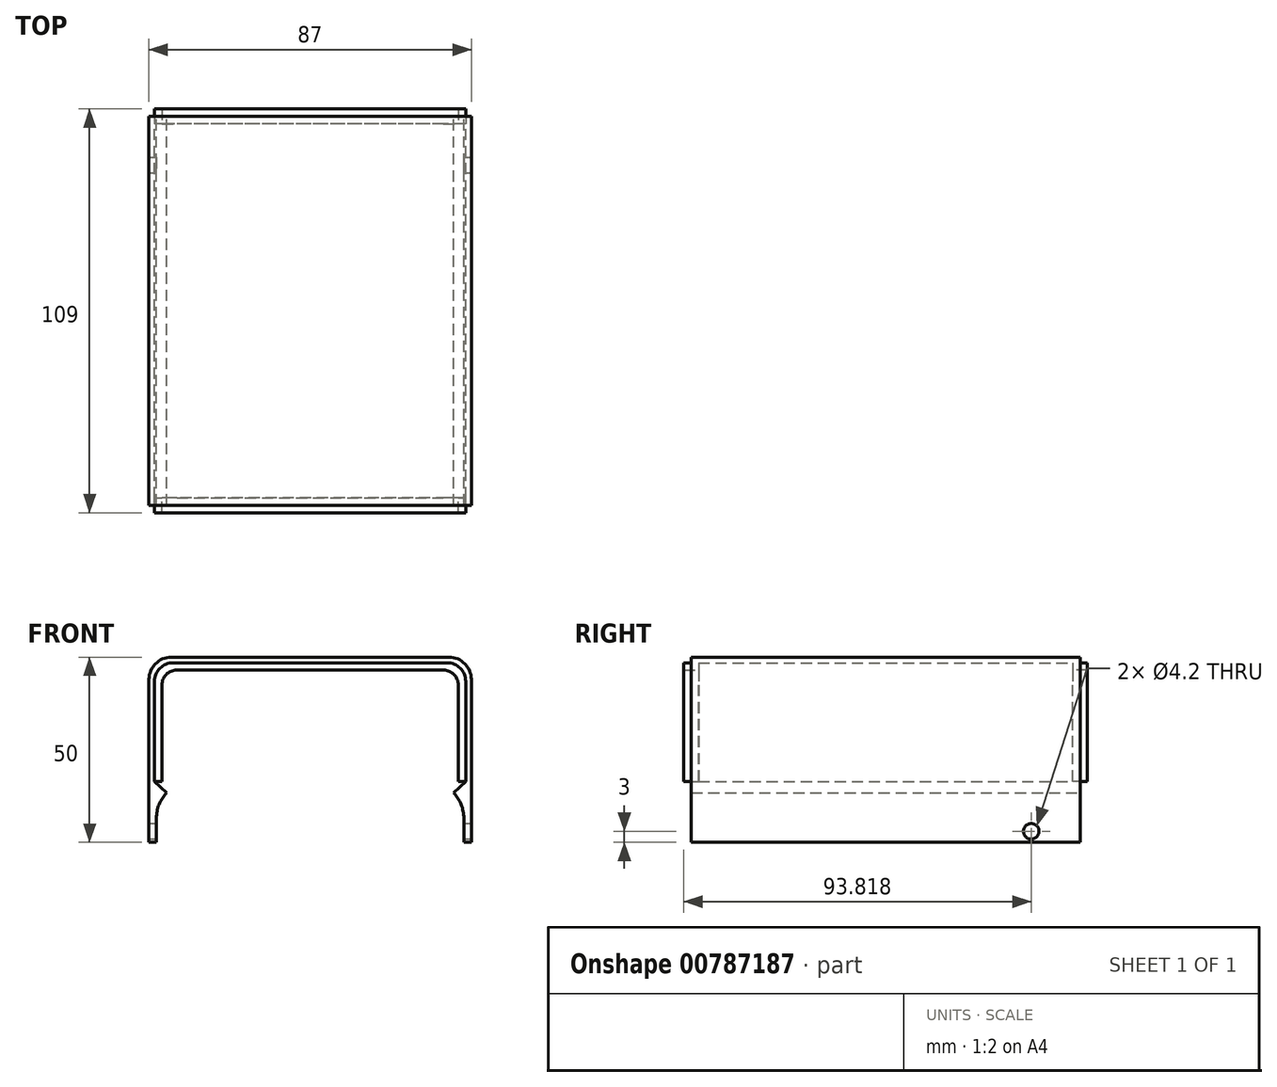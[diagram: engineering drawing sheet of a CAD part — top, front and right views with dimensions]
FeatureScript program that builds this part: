
annotation { "Feature Type Name" : "Feature", "Feature Type Description" : "" }
export const myFeature = defineFeature(function(context is Context, id is Id, definition is map)
    precondition{}
    {
        {
            var Q0;
            Q0=qCreatedBy(makeId("Front.planeOp"),FACE);
            var sketch = newSketch(context, id + "F0", { "sketchPlane" : qUnion([Q0])});
            skLineSegment(sketch, "E0.bottom", {"start": v(-31.5, 21.5) * mm, "end": v(31.5, 21.5) * mm});
            skLineSegment(sketch, "E0.top", {"start": v(-41.5, -21.5) * mm, "end": v(41.5, -21.5) * mm});
            skLineSegment(sketch, "E0.left", {"start": v(-41.5, 11.5) * mm, "end": v(-41.5, -21.5) * mm});
            skLineSegment(sketch, "E0.right", {"start": v(41.5, 11.5) * mm, "end": v(41.5, -21.5) * mm});
            skPoint(sketch, "E0.middle", {"position": v(0, 0) * mm});
            skPoint(sketch, "E1.visualSharp", {"position": v(-41.5, 21.5) * mm});
            skArc(sketch, "E1.filletArc", {"start": v(-31.5, 21.5) * mm, "mid": v(-38.57, 18.57) * mm, "end": v(-41.5, 11.5) * mm});
            skPoint(sketch, "E2.visualSharp", {"position": v(41.5, 21.5) * mm});
            skArc(sketch, "E2.filletArc", {"start": v(41.5, 11.5) * mm, "mid": v(38.57, 18.57) * mm, "end": v(31.5, 21.5) * mm});
            skLineSegment(sketch, "E3", {"start": v(-41.5, 5) * mm, "end": v(-43.5, 5) * mm});
            skLineSegment(sketch, "E4", {"start": v(-43.5, 49) * mm, "end": v(-43.5, 5) * mm});
            skLineSegment(sketch, "E5", {"start": v(41.5, 5) * mm, "end": v(43.5, 5) * mm});
            skLineSegment(sketch, "E6", {"start": v(43.5, 49) * mm, "end": v(43.5, 5) * mm});
            skLineSegment(sketch, "E7", {"start": v(37.5, 55) * mm, "end": v(-37.5, 55) * mm});
            skLineSegment(sketch, "E8", {"start": v(-31.5, 21.5) * mm, "end": v(-42, 21.5) * mm});
            skLineSegment(sketch, "E9", {"start": v(-42, 21.5) * mm, "end": v(-42, 48.5) * mm});
            skLineSegment(sketch, "E10", {"start": v(31.5, 21.5) * mm, "end": v(42, 21.5) * mm});
            skLineSegment(sketch, "E11", {"start": v(42, 21.5) * mm, "end": v(42, 48.5) * mm});
            skLineSegment(sketch, "E12", {"start": v(37, 53.5) * mm, "end": v(-37, 53.5) * mm});
            skPoint(sketch, "E13.visualSharp", {"position": v(-42, 53.5) * mm});
            skArc(sketch, "E13.filletArc", {"start": v(-37, 53.5) * mm, "mid": v(-40.54, 52.04) * mm, "end": v(-42, 48.5) * mm});
            skPoint(sketch, "E14.visualSharp", {"position": v(42, 53.5) * mm});
            skArc(sketch, "E14.filletArc", {"start": v(42, 48.5) * mm, "mid": v(40.54, 52.04) * mm, "end": v(37, 53.5) * mm});
            skPoint(sketch, "E15.visualSharp", {"position": v(-43.5, 55) * mm});
            skArc(sketch, "E15.filletArc", {"start": v(-37.5, 55) * mm, "mid": v(-41.74, 53.24) * mm, "end": v(-43.5, 49) * mm});
            skPoint(sketch, "E16.visualSharp", {"position": v(43.5, 55) * mm});
            skArc(sketch, "E16.filletArc", {"start": v(43.5, 49) * mm, "mid": v(41.74, 53.24) * mm, "end": v(37.5, 55) * mm});
            skLineSegment(sketch, "E17", {"start": v(-42, 21.5) * mm, "end": v(-31.5, 11.5) * mm});
            skLineSegment(sketch, "E18", {"start": v(42, 21.5) * mm, "end": v(31.5, 11.5) * mm});
            skSolve(sketch);
        }
        {
            var Q0;
            {var subQ2=sQuery(id+"F0.wireOp",EDGE,"E3");Q0=makeQuery(id+"F0.imprint","IMPRINT",FACE,{"disambiguationData":[TD([[makeQuery(id+"F0.imprint","IMPRINT",EDGE,{"derivedFrom":subQ2}),-1.0]])]});}
            extrude(context, id + "F1", {"entities" : qUnion([Q0]), "depth" : 105 * mm, "offsetDistance" : 25 * mm});
        }
        {
            var Q0;
            Q0=makeQuery(id+"F1.opExtrude","SWEPT_FACE",FACE,{"disambiguationData":[OSD([sQuery(id+"F0.wireOp",EDGE,"E6")])]});
            var sketch = newSketch(context, id + "F2", { "sketchPlane" : qUnion([Q0])});
            skCircle(sketch, "E19", {"center": v(-13.18, 8) * mm, "radius": 2.1 * mm});
            skSolve(sketch);
        }
        {
            var Q0;
            Q0=makeQuery(id+"F2.imprint","IMPRINT",FACE,{"disambiguationData":[TD([[makeQuery(id+"F2.imprint","IMPRINT",EDGE,{"derivedFrom":sQuery(id+"F2.wireOp",EDGE,"E19")}),1.0]])]});
            extrude(context, id + "F3", {"entities" : qUnion([Q0]), "operationType" : NewBodyOperationType.REMOVE, "endBound" : BoundingType.THROUGH_ALL, "oppositeDirection" : true, "depth" : 25 * mm, "offsetDistance" : 25 * mm});
        }
        {
            var Q0;
            Q0=makeQuery(id+"F1.opExtrude","CAP_FACE",FACE,{"disambiguationData":[OSD([sQuery(id+"F0.wireOp",EDGE,"E0.left"),sQuery(id+"F0.wireOp",EDGE,"E0.right"),sQuery(id+"F0.wireOp",EDGE,"E1.filletArc"),sQuery(id+"F0.wireOp",EDGE,"E2.filletArc"),sQuery(id+"F0.wireOp",EDGE,"E3"),sQuery(id+"F0.wireOp",EDGE,"E4"),sQuery(id+"F0.wireOp",EDGE,"E5"),sQuery(id+"F0.wireOp",EDGE,"E6"),sQuery(id+"F0.wireOp",EDGE,"E7"),sQuery(id+"F0.wireOp",EDGE,"E9"),sQuery(id+"F0.wireOp",EDGE,"E11"),sQuery(id+"F0.wireOp",EDGE,"E12"),sQuery(id+"F0.wireOp",EDGE,"E13.filletArc"),sQuery(id+"F0.wireOp",EDGE,"E14.filletArc"),sQuery(id+"F0.wireOp",EDGE,"E15.filletArc"),sQuery(id+"F0.wireOp",EDGE,"E16.filletArc"),sQuery(id+"F0.wireOp",EDGE,"E17"),sQuery(id+"F0.wireOp",EDGE,"E18")])],"isStart":true});
            var sketch = newSketch(context, id + "F4", { "sketchPlane" : qUnion([Q0])});
            skLineSegment(sketch, "E20.0", {"start": v(-37.5, 55) * mm, "end": v(37.5, 55) * mm});
            skArc(sketch, "E21.0", {"start": v(-43.5, 49) * mm, "mid": v(-41.74, 53.24) * mm, "end": v(-37.5, 55) * mm});
            skArc(sketch, "E22.0", {"start": v(37.5, 55) * mm, "mid": v(41.74, 53.24) * mm, "end": v(43.5, 49) * mm});
            skLineSegment(sketch, "E23.0", {"start": v(-43.5, 49) * mm, "end": v(-43.5, 5) * mm});
            skLineSegment(sketch, "E24.0", {"start": v(43.5, 49) * mm, "end": v(43.5, 5) * mm});
            skLineSegment(sketch, "E25", {"start": v(-43.5, 5) * mm, "end": v(43.5, 5) * mm});
            skSolve(sketch);
        }
        {
            var Q0;
            Q0=makeQuery(id+"F1.opExtrude","CAP_FACE",FACE,{"disambiguationData":[OSD([sQuery(id+"F0.wireOp",EDGE,"E0.left"),sQuery(id+"F0.wireOp",EDGE,"E0.right"),sQuery(id+"F0.wireOp",EDGE,"E1.filletArc"),sQuery(id+"F0.wireOp",EDGE,"E2.filletArc"),sQuery(id+"F0.wireOp",EDGE,"E3"),sQuery(id+"F0.wireOp",EDGE,"E4"),sQuery(id+"F0.wireOp",EDGE,"E5"),sQuery(id+"F0.wireOp",EDGE,"E6"),sQuery(id+"F0.wireOp",EDGE,"E7"),sQuery(id+"F0.wireOp",EDGE,"E9"),sQuery(id+"F0.wireOp",EDGE,"E11"),sQuery(id+"F0.wireOp",EDGE,"E12"),sQuery(id+"F0.wireOp",EDGE,"E13.filletArc"),sQuery(id+"F0.wireOp",EDGE,"E14.filletArc"),sQuery(id+"F0.wireOp",EDGE,"E15.filletArc"),sQuery(id+"F0.wireOp",EDGE,"E16.filletArc"),sQuery(id+"F0.wireOp",EDGE,"E17"),sQuery(id+"F0.wireOp",EDGE,"E18")])],"isStart":false});
            var sketch = newSketch(context, id + "F5", { "sketchPlane" : qUnion([Q0])});
            skLineSegment(sketch, "E26.0.0", {"start": v(-31.5, 21.5) * mm, "end": v(31.5, 21.5) * mm});
            skLineSegment(sketch, "E26.0.1", {"start": v(31.5, 21.5) * mm, "end": v(42, 21.5) * mm});
            skLineSegment(sketch, "E26.0.2", {"start": v(42, 21.5) * mm, "end": v(42, 48.5) * mm});
            skArc(sketch, "E26.0.3", {"start": v(42, 48.5) * mm, "mid": v(40.54, 52.04) * mm, "end": v(37, 53.5) * mm});
            skLineSegment(sketch, "E26.0.4", {"start": v(37, 53.5) * mm, "end": v(-37, 53.5) * mm});
            skArc(sketch, "E26.0.5", {"start": v(-37, 53.5) * mm, "mid": v(-40.54, 52.04) * mm, "end": v(-42, 48.5) * mm});
            skLineSegment(sketch, "E26.0.6", {"start": v(-42, 48.5) * mm, "end": v(-42, 21.5) * mm});
            skLineSegment(sketch, "E26.0.7", {"start": v(-42, 21.5) * mm, "end": v(-31.5, 21.5) * mm});
            skLineSegment(sketch, "E27", {"start": v(-40, 21.5) * mm, "end": v(-40, 47.5) * mm});
            skLineSegment(sketch, "E28", {"start": v(-36, 51.5) * mm, "end": v(36, 51.5) * mm});
            skLineSegment(sketch, "E29", {"start": v(40, 47.5) * mm, "end": v(40, 21.5) * mm});
            skPoint(sketch, "E30.visualSharp", {"position": v(-40, 51.5) * mm});
            skArc(sketch, "E30.filletArc", {"start": v(-36, 51.5) * mm, "mid": v(-38.83, 50.33) * mm, "end": v(-40, 47.5) * mm});
            skPoint(sketch, "E31.visualSharp", {"position": v(40, 51.5) * mm});
            skArc(sketch, "E31.filletArc", {"start": v(40, 47.5) * mm, "mid": v(38.83, 50.33) * mm, "end": v(36, 51.5) * mm});
            skSolve(sketch);
        }
        {
            var Q0;
            {var subQ4=sQuery(id+"F5.wireOp",EDGE,"E26.0.2");Q0=makeQuery(id+"F5.imprint","IMPRINT",FACE,{"disambiguationData":[TD([[makeQuery(id+"F5.imprint","IMPRINT",EDGE,{"derivedFrom":subQ4}),1.0]])]});}
            extrude(context, id + "F6", {"entities" : qUnion([Q0]), "operationType" : NewBodyOperationType.ADD, "endBound" : BoundingType.SYMMETRIC, "depth" : 4 * mm, "offsetDistance" : 25 * mm});
        }
        {
            var Q0;
            Q0=makeQuery(id+"F4.imprint","IMPRINT",FACE,{"disambiguationData":[TD([[makeQuery(id+"F4.imprint","IMPRINT",EDGE,{"derivedFrom":sQuery(id+"F4.wireOp",EDGE,"E20.0")}),-1.0]])]});
            var sketch = newSketch(context, id + "F7", { "sketchPlane" : qUnion([Q0])});
            skLineSegment(sketch, "E32.0", {"start": v(-42, 21.5) * mm, "end": v(-42, 48.5) * mm});
            skArc(sketch, "E33.0", {"start": v(-42, 48.5) * mm, "mid": v(-40.54, 52.04) * mm, "end": v(-37, 53.5) * mm});
            skLineSegment(sketch, "E34.0", {"start": v(-37, 53.5) * mm, "end": v(37, 53.5) * mm});
            skArc(sketch, "E35.0", {"start": v(37, 53.5) * mm, "mid": v(40.54, 52.04) * mm, "end": v(42, 48.5) * mm});
            skLineSegment(sketch, "E36.0", {"start": v(42, 21.5) * mm, "end": v(42, 48.5) * mm});
            skLineSegment(sketch, "E37", {"start": v(-40, 21.5) * mm, "end": v(-40, 47.5) * mm});
            skLineSegment(sketch, "E38", {"start": v(-36, 51.5) * mm, "end": v(36, 51.5) * mm});
            skLineSegment(sketch, "E39", {"start": v(40, 47.5) * mm, "end": v(40, 21.5) * mm});
            skPoint(sketch, "E40.visualSharp", {"position": v(-40, 51.5) * mm});
            skArc(sketch, "E40.filletArc", {"start": v(-36, 51.5) * mm, "mid": v(-38.83, 50.33) * mm, "end": v(-40, 47.5) * mm});
            skPoint(sketch, "E41.visualSharp", {"position": v(40, 51.5) * mm});
            skArc(sketch, "E41.filletArc", {"start": v(40, 47.5) * mm, "mid": v(38.83, 50.33) * mm, "end": v(36, 51.5) * mm});
            skLineSegment(sketch, "E42", {"start": v(-42, 21.5) * mm, "end": v(42, 21.5) * mm});
            skSolve(sketch);
        }
        {
            var Q0;
            {var subQ3=sQuery(id+"F7.wireOp",EDGE,"E32.0");Q0=makeQuery(id+"F7.imprint","IMPRINT",FACE,{"disambiguationData":[TD([[makeQuery(id+"F7.imprint","IMPRINT",EDGE,{"derivedFrom":subQ3}),-1.0]])]});}
            extrude(context, id + "F8", {"entities" : qUnion([Q0]), "operationType" : NewBodyOperationType.ADD, "endBound" : BoundingType.SYMMETRIC, "depth" : 4 * mm, "offsetDistance" : 25 * mm});
        }
    });
